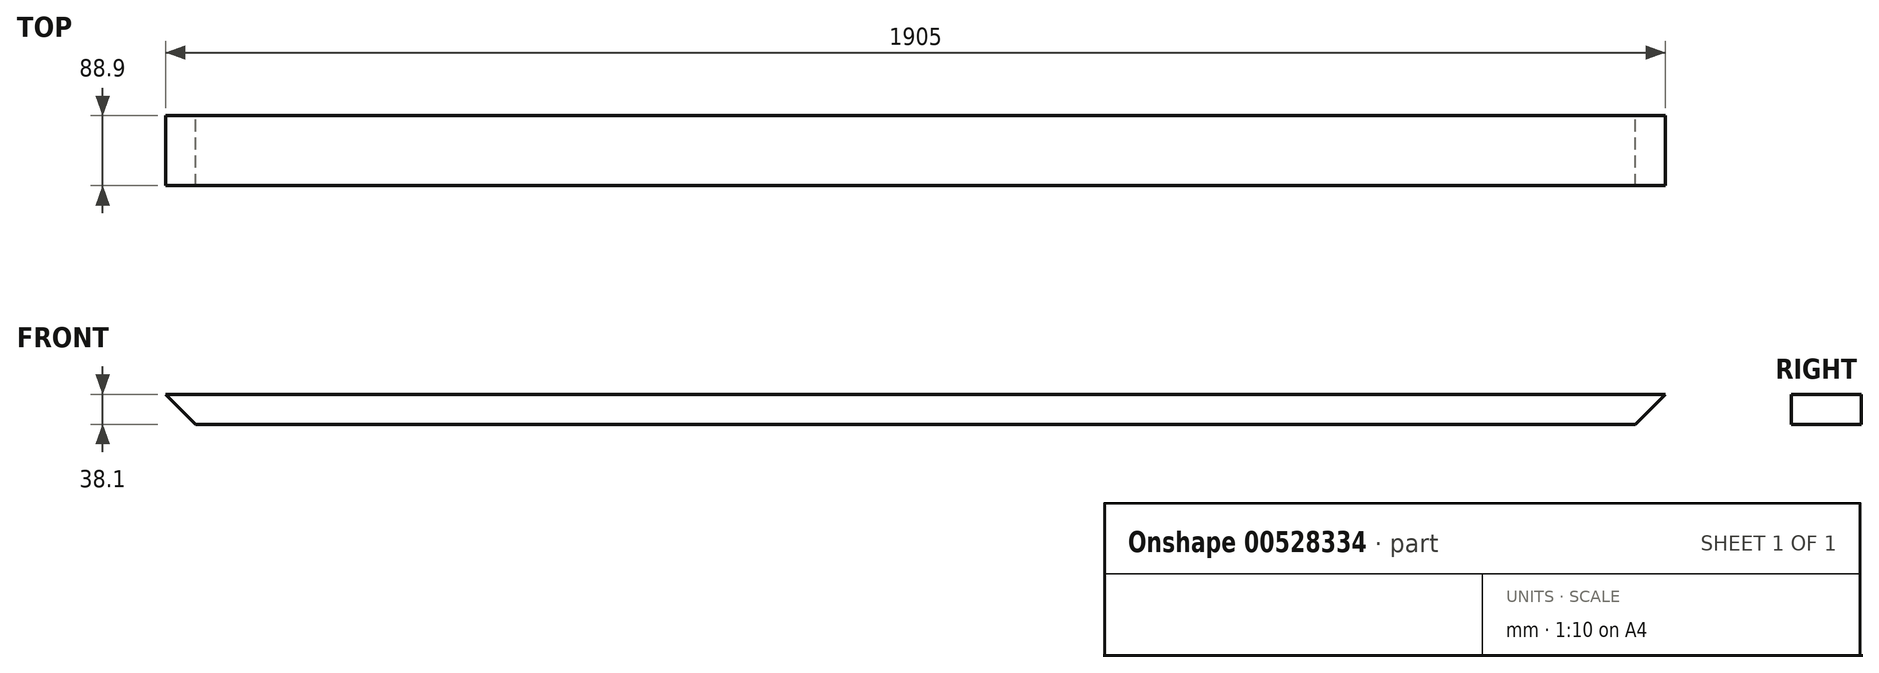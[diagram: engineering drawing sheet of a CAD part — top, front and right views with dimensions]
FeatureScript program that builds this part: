
annotation { "Feature Type Name" : "Feature", "Feature Type Description" : "" }
export const myFeature = defineFeature(function(context is Context, id is Id, definition is map)
    precondition{}
    {
        {
            var Q0;
            Q0=qCreatedBy(makeId("Front.planeOp"),FACE);
            var sketch = newSketch(context, id + "F0", { "sketchPlane" : qUnion([Q0])});
            skLineSegment(sketch, "E0", {"start": v(0, 0) * mm, "end": v(1905, 0) * mm});
            skLineSegment(sketch, "E1", {"start": v(1905, 0) * mm, "end": v(1905, -38.1) * mm, "construction": true});
            skLineSegment(sketch, "E2", {"start": v(0, -1.5) * mm, "end": v(0, 0) * mm, "construction": true});
            skLineSegment(sketch, "E3", {"start": v(1905, 0) * mm, "end": v(1866.9, -38.1) * mm});
            skLineSegment(sketch, "E4", {"start": v(0, 0) * mm, "end": v(38.1, -38.1) * mm});
            skLineSegment(sketch, "E5", {"start": v(38.1, -38.1) * mm, "end": v(1866.9, -38.1) * mm});
            skSolve(sketch);
        }
        {
            var Q0;
            Q0 = qSketchRegion(id + "F0", true);
            extrude(context, id + "F1", {"entities" : qUnion([Q0]), "depth" : 88.9 * mm, "offsetDistance" : 25 * mm});
        }
    });
